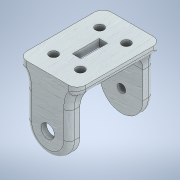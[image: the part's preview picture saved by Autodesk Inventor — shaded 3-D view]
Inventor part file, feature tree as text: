
AUTODESK INVENTOR PART (.ipt)
format: ipt  version: 2021 (Build 250183000, 183)  size: 529,408 bytes
history: native  units: mm
features: extrude x12, sketch x12, fillet x6, projected_geometry x5, plane x1, pattern_linear x1
ambient origin geometry x8: Origin, YZ Plane, XZ Plane, XY Plane, X Axis, Y Axis, Z Axis, Center Point
bodies: Solid1 (feature_tree)
feature tree (37):
  extrude  "Extrusion1"  Depth=40.0mm
  extrude  "Extrusion2"  Depth=5.0mm TaperAngle=0.0deg
  extrude  "Extrusion3"  Depth=5.0mm TaperAngle=0.0deg
  fillet  "Fillet1"  Radius=2.0mm
  plane  "Work Plane1"
  extrude  "Extrusion4"  Depth=59.0mm
  extrude  "Extrusion5"  Depth=7.0mm TaperAngle=0.0deg
  fillet  "Fillet2"  Radius=3.0mm
  extrude  "Extrusion6"  Depth=7.5mm
  pattern_linear  "Rectangular Pattern1"  Count1=2 Spacing1=66.0mm
  extrude  "Extrusion7"  Depth=5.0mm
  fillet  "Fillet3"  Radius=5.0mm
  fillet  "Fillet4"  Radius=15.0mm
  fillet  "Fillet5"  Radius=8.0mm
  extrude  "Extrusion8"  Depth=8.0mm
  extrude  "Extrusion9"  Depth=8.0mm
  extrude  "Extrusion10"  Depth=15.0mm
  extrude  "Extrusion11"  Depth=15.0mm
  extrude  "Extrusion12"  Depth=15.0mm
  fillet  "Fillet6"  Radius=15.0mm
  sketch  "Sketch1"  dims[d0=30.0mm d1=40.0mm]
  sketch  "Sketch2"  dims[d2=40.0mm d3=5.0mm d4=0.0mm]
  projected_geometry  "Projected Loop1"
  sketch  "Sketch3"  dims[d5=12.5mm d6=5.0mm d7=0.0mm d8=2.0mm d9=0.0mm]
  projected_geometry  "Projected Loop2"
  sketch  "Sketch4"  dims[d10=5.0mm d11=59.0mm]
  projected_geometry  "Projected Loop3"
  sketch  "Sketch5"  dims[d12=7.8mm d13=7.0mm d14=0.0mm d15=3.0mm d16=0.0mm]
  sketch  "Sketch6"  dims[d17=10.0mm d18=7.5mm]
  sketch  "Sketch7"  dims[d19=7.5mm]
  sketch  "Sketch8"  dims[d20=15.0mm]
  sketch  "Sketch9"  dims[d21=15.0mm]
  sketch  "Sketch11"  dims[d22=3.0mm d23=0.0mm d24=20.0mm d26=66.0mm]
  projected_geometry  "Projected Loop5"
  sketch  "Sketch12"  dims[d27=7.0mm d28=0.0mm d29=5.0mm d30=5.0mm d31=15.0mm d32=8.0mm]
  projected_geometry  "Projected Loop6"
  sketch  "Sketch14"  dims[d33=8.0mm d34=8.0mm d35=8.0mm d36=15.0mm d37=15.0mm d38=15.0mm d39=15.0mm d40=15.0mm d41=15.0mm d42=15.0mm d43=15.0mm d44=8.0mm d45=25.0mm d46=23.5mm d47=24.0mm d48=20.0mm d49=0.0mm d50=15.0mm d51=15.0mm d52=15.0mm d53=15.0mm d54=20.0mm d55=0.0mm d56=10.0mm d57=0.0mm d58=10.0mm d59=0.0mm d60=8.0mm d61=15.0mm d62=0.0mm d63=5.0mm]
